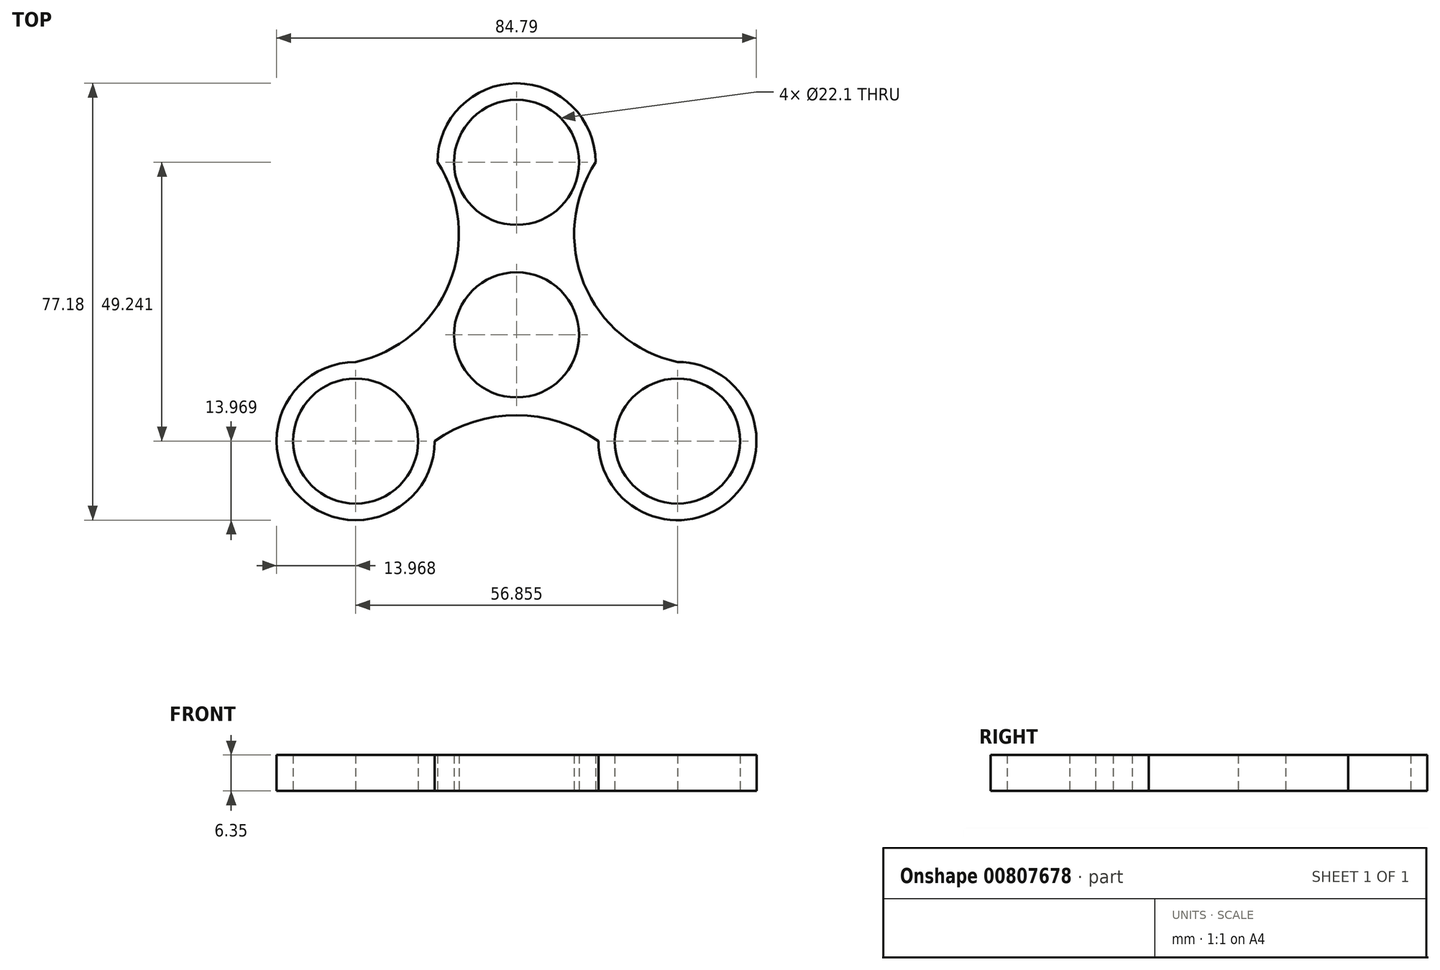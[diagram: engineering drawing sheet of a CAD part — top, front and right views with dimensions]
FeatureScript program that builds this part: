
annotation { "Feature Type Name" : "Feature", "Feature Type Description" : "" }
export const myFeature = defineFeature(function(context is Context, id is Id, definition is map)
    precondition{}
    {
        {
            var Q0;
            Q0=qCreatedBy(makeId("Top.planeOp"),FACE);
            var sketch = newSketch(context, id + "F0", { "sketchPlane" : qUnion([Q0])});
            skCircle(sketch, "E0", {"center": v(0, 0) * mm, "radius": 44.45 * mm});
            skCircle(sketch, "E1", {"center": v(0, 0) * mm, "radius": 11.05 * mm});
            skLineSegment(sketch, "E2", {"start": v(0, 0) * mm, "end": v(0, 30.48) * mm});
            skCircle(sketch, "E3", {"center": v(0, 30.48) * mm, "radius": 11.05 * mm});
            skCircle(sketch, "E4.1.0", {"center": v(-28.43, -18.76) * mm, "radius": 11.05 * mm});
            skCircle(sketch, "E4.2.0", {"center": v(28.42, -18.76) * mm, "radius": 11.05 * mm});
            skPoint(sketch, "E4.center", {"position": v(0, -2.35) * mm});
            skCircle(sketch, "E5", {"center": v(0, 30.48) * mm, "radius": 13.97 * mm});
            skCircle(sketch, "E6", {"center": v(28.42, -18.76) * mm, "radius": 13.97 * mm});
            skCircle(sketch, "E7", {"center": v(-28.43, -18.76) * mm, "radius": 13.97 * mm});
            skCircle(sketch, "E8", {"center": v(0, 0) * mm, "radius": 13.97 * mm});
            skArc(sketch, "E9", {"start": v(-28.43, -4.79) * mm, "mid": v(-11.9, 9.04) * mm, "end": v(-13.97, 30.48) * mm});
            skArc(sketch, "E10", {"start": v(13.97, 30.48) * mm, "mid": v(11.9, 9.04) * mm, "end": v(28.42, -4.8) * mm});
            skArc(sketch, "E11", {"start": v(14.45, -18.76) * mm, "mid": v(0, -14.2) * mm, "end": v(-14.46, -18.76) * mm});
            skSolve(sketch);
        }
        {
            var Q0;
            Q0=makeQuery(id+"F0.imprint","IMPRINT",FACE,{"disambiguationData":[TD([[makeQuery(id+"F0.imprint","IMPRINT",EDGE,{"derivedFrom":sQuery(id+"F0.wireOp",EDGE,"E3")}),-1.0]])]});
            var Q1;
            Q1=makeQuery(id+"F0.imprint","IMPRINT",FACE,{"disambiguationData":[TD([[makeQuery(id+"F0.imprint","IMPRINT",EDGE,{"derivedFrom":sQuery(id+"F0.wireOp",EDGE,"E1")}),-1.0]])]});
            var Q2;
            {var subQ0=sQuery(id+"F0.wireOp",EDGE,"E6");var subQ2=sQuery(id+"F0.wireOp",EDGE,"E0");var subQ7=makeQuery(id+"F0.imprint","INTERSECT",VERTEX,{"disambiguationData":[OD(0.0)],"derivedFrom":[subQ2,subQ0]});Q2=makeQuery(id+"F0.imprint","IMPRINT",FACE,{"disambiguationData":[TD([[makeQuery(id+"F0.imprint","IMPRINT",EDGE,{"disambiguationData":[TD([[subQ7,-1.0]])],"derivedFrom":subQ2}),1.0]])]});}
            var Q3;
            {var subQ0=sQuery(id+"F0.wireOp",EDGE,"E6");var subQ1=sQuery(id+"F0.wireOp",EDGE,"E0");var subQ2=makeQuery(id+"F0.imprint","INTERSECT",VERTEX,{"disambiguationData":[OD(0.0)],"derivedFrom":[subQ1,subQ0]});Q3=makeQuery(id+"F0.imprint","IMPRINT",FACE,{"disambiguationData":[TD([[makeQuery(id+"F0.imprint","IMPRINT",EDGE,{"disambiguationData":[TD([[subQ2,-1.0]])],"derivedFrom":subQ1}),-1.0]])]});}
            var Q4;
            Q4=makeQuery(id+"F0.imprint","IMPRINT",FACE,{"disambiguationData":[TD([[makeQuery(id+"F0.imprint","IMPRINT",EDGE,{"derivedFrom":sQuery(id+"F0.wireOp",EDGE,"E8")}),-1.0]])]});
            var Q5;
            {var subQ0=sQuery(id+"F0.wireOp",EDGE,"E7");var subQ3=sQuery(id+"F0.wireOp",EDGE,"E0");var subQ8=makeQuery(id+"F0.imprint","INTERSECT",VERTEX,{"disambiguationData":[OD(0.0)],"derivedFrom":[subQ3,subQ0]});Q5=makeQuery(id+"F0.imprint","IMPRINT",FACE,{"disambiguationData":[TD([[makeQuery(id+"F0.imprint","IMPRINT",EDGE,{"disambiguationData":[TD([[subQ8,-1.0]])],"derivedFrom":subQ3}),1.0]])]});}
            var Q6;
            {var subQ0=sQuery(id+"F0.wireOp",EDGE,"E7");var subQ1=sQuery(id+"F0.wireOp",EDGE,"E0");var subQ2=makeQuery(id+"F0.imprint","INTERSECT",VERTEX,{"disambiguationData":[OD(0.0)],"derivedFrom":[subQ1,subQ0]});Q6=makeQuery(id+"F0.imprint","IMPRINT",FACE,{"disambiguationData":[TD([[makeQuery(id+"F0.imprint","IMPRINT",EDGE,{"disambiguationData":[TD([[subQ2,-1.0]])],"derivedFrom":subQ1}),-1.0]])]});}
            extrude(context, id + "F1", {"entities" : qUnion([Q0, Q1, Q2, Q3, Q4, Q5, Q6]), "depth" : 6.35 * mm, "offsetDistance" : 25.4 * mm});
        }
    });
